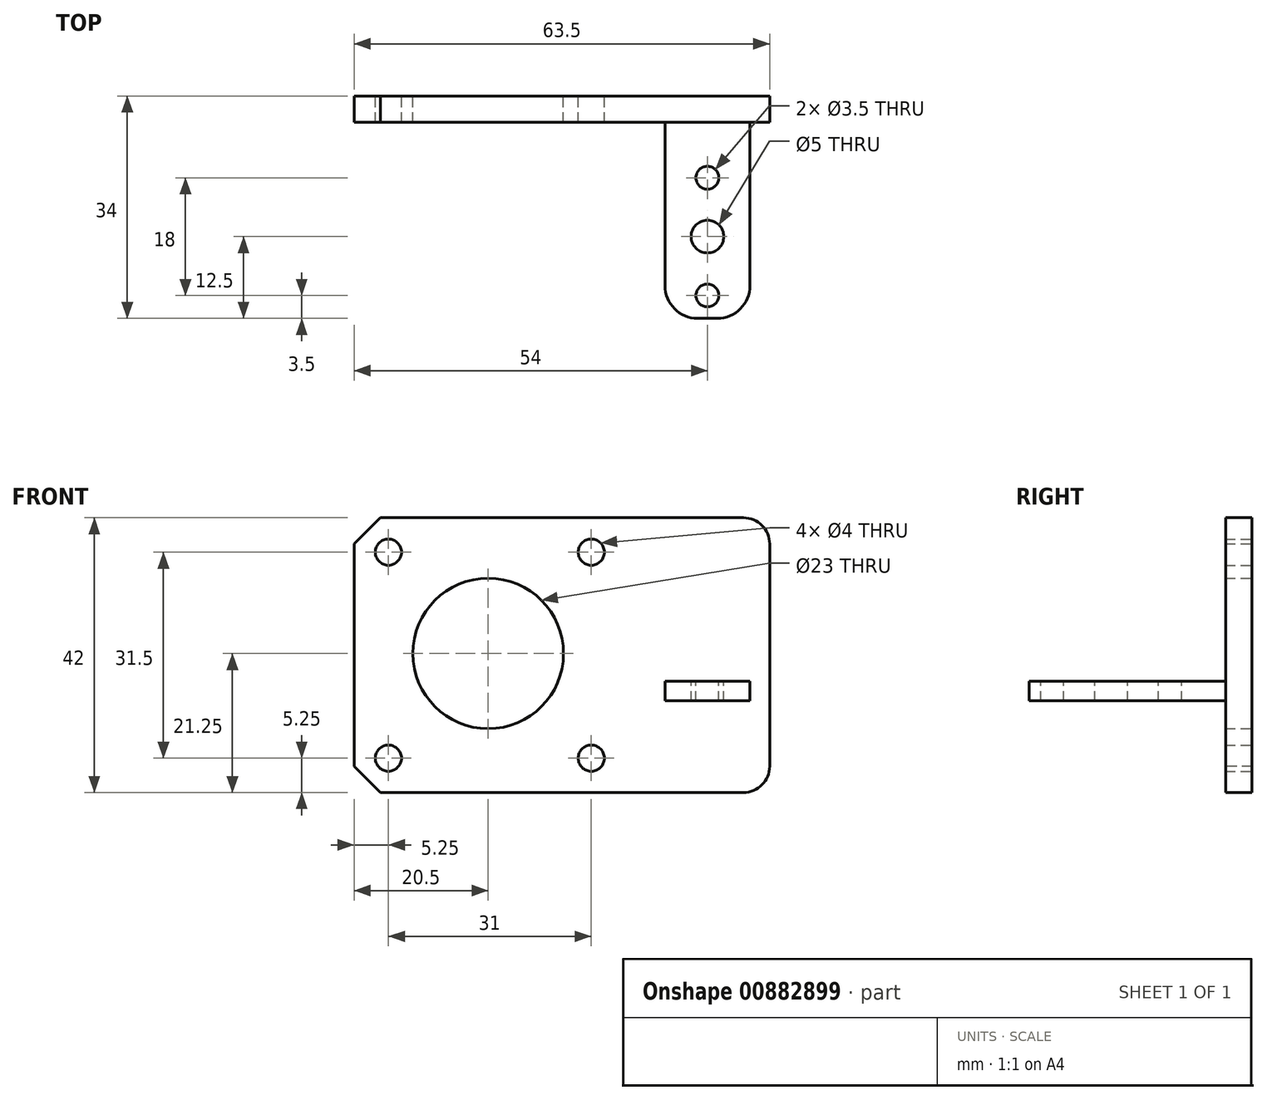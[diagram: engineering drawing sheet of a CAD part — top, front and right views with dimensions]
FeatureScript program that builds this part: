
annotation { "Feature Type Name" : "Feature", "Feature Type Description" : "" }
export const myFeature = defineFeature(function(context is Context, id is Id, definition is map)
    precondition{}
    {
        {
            var Q0;
            Q0=qCreatedBy(makeId("Front.planeOp"),FACE);
            var sketch = newSketch(context, id + "F0", { "sketchPlane" : qUnion([Q0])});
            skLineSegment(sketch, "E0.bottom", {"start": v(43, -21.25) * mm, "end": v(-20.5, -21.25) * mm});
            skLineSegment(sketch, "E0.top", {"start": v(43, 20.75) * mm, "end": v(-20.5, 20.75) * mm});
            skLineSegment(sketch, "E0.left", {"start": v(43, -21.25) * mm, "end": v(43, 20.75) * mm});
            skLineSegment(sketch, "E0.right", {"start": v(-20.5, -21.25) * mm, "end": v(-20.5, 20.75) * mm});
            skPoint(sketch, "E0.middle", {"position": v(0, 0) * mm});
            skCircle(sketch, "E1", {"center": v(0, 0) * mm, "radius": 11.5 * mm});
            skCircle(sketch, "E2", {"center": v(-15.25, 15.5) * mm, "radius": 2 * mm});
            skCircle(sketch, "E3", {"center": v(15.75, 15.5) * mm, "radius": 2 * mm});
            skCircle(sketch, "E4", {"center": v(-15.25, -16) * mm, "radius": 2 * mm});
            skCircle(sketch, "E5", {"center": v(15.75, -16) * mm, "radius": 2 * mm});
            skSolve(sketch);
        }
        {
            var Q0;
            Q0=makeQuery(id+"F0.imprint","IMPRINT",FACE,{"disambiguationData":[TD([[makeQuery(id+"F0.imprint","IMPRINT",EDGE,{"derivedFrom":sQuery(id+"F0.wireOp",EDGE,"E0.bottom")}),-1.0]])]});
            extrude(context, id + "F1", {"entities" : qUnion([Q0]), "depth" : 4 * mm, "offsetDistance" : 25 * mm});
        }
        {
            var Q0;
            Q0=makeQuery(id+"F1.opExtrude","SWEPT_EDGE",EDGE,{"disambiguationData":[OSD([sQuery(id+"F0.wireOp",EDGE,"E0.bottom"),sQuery(id+"F0.wireOp",EDGE,"E0.right")])]});
            var Q1;
            Q1=makeQuery(id+"F1.opExtrude","SWEPT_EDGE",EDGE,{"disambiguationData":[OSD([sQuery(id+"F0.wireOp",EDGE,"E0.top"),sQuery(id+"F0.wireOp",EDGE,"E0.right")])]});
            chamfer(context, id + "F2", {"entities" : qUnion([Q0, Q1]), "width" : 4 * mm, "tangentPropagation" : true});
        }
        {
            var Q0;
            Q0=makeQuery(id+"F1.opExtrude","CAP_FACE",FACE,{"disambiguationData":[OSD([sQuery(id+"F0.wireOp",EDGE,"E0.bottom"),sQuery(id+"F0.wireOp",EDGE,"E0.top"),sQuery(id+"F0.wireOp",EDGE,"E0.left"),sQuery(id+"F0.wireOp",EDGE,"E0.right"),sQuery(id+"F0.wireOp",EDGE,"E1"),sQuery(id+"F0.wireOp",EDGE,"E2"),sQuery(id+"F0.wireOp",EDGE,"E3"),sQuery(id+"F0.wireOp",EDGE,"E4"),sQuery(id+"F0.wireOp",EDGE,"E5")])],"isStart":false});
            var sketch = newSketch(context, id + "F3", { "sketchPlane" : qUnion([Q0])});
            skLineSegment(sketch, "E6.bottom", {"start": v(27, -4.25) * mm, "end": v(40, -4.25) * mm});
            skLineSegment(sketch, "E6.top", {"start": v(27, -7.25) * mm, "end": v(40, -7.25) * mm});
            skLineSegment(sketch, "E6.left", {"start": v(27, -4.25) * mm, "end": v(27, -7.25) * mm});
            skLineSegment(sketch, "E6.right", {"start": v(40, -4.25) * mm, "end": v(40, -7.25) * mm});
            skSolve(sketch);
        }
        {
            var Q0;
            Q0 = qSketchRegion(id + "F3", true);
            extrude(context, id + "F4", {"entities" : qUnion([Q0]), "operationType" : NewBodyOperationType.ADD, "depth" : 30 * mm, "offsetDistance" : 25 * mm});
        }
        {
            var Q0;
            Q0=makeQuery(id+"F4.opExtrude","CAP_EDGE",EDGE,{"disambiguationData":[OSD([sQuery(id+"F3.wireOp",EDGE,"E6.right")])],"isStart":false});
            var Q1;
            Q1=makeQuery(id+"F4.opExtrude","CAP_EDGE",EDGE,{"disambiguationData":[OSD([sQuery(id+"F3.wireOp",EDGE,"E6.left")])],"isStart":false});
            fillet(context, id + "F5", {"entities" : qUnion([Q0, Q1]), "radius" : 5 * mm, "tangentPropagation" : true, "allowEdgeOverflow" : false});
        }
        {
            var Q0;
            Q0=makeQuery(id+"F1.opExtrude","SWEPT_EDGE",EDGE,{"disambiguationData":[OSD([sQuery(id+"F0.wireOp",EDGE,"E0.top"),sQuery(id+"F0.wireOp",EDGE,"E0.left")])]});
            var Q1;
            Q1=makeQuery(id+"F1.opExtrude","SWEPT_EDGE",EDGE,{"disambiguationData":[OSD([sQuery(id+"F0.wireOp",EDGE,"E0.bottom"),sQuery(id+"F0.wireOp",EDGE,"E0.left")])]});
            fillet(context, id + "F6", {"entities" : qUnion([Q0, Q1]), "radius" : 4 * mm, "tangentPropagation" : true, "allowEdgeOverflow" : false});
        }
        {
            var Q0;
            Q0=makeQuery(id+"F4.opExtrude","SWEPT_FACE",FACE,{"disambiguationData":[OSD([sQuery(id+"F3.wireOp",EDGE,"E6.bottom")])]});
            var sketch = newSketch(context, id + "F7", { "sketchPlane" : qUnion([Q0])});
            skCircle(sketch, "E7", {"center": v(33.5, -21.5) * mm, "radius": 2.5 * mm});
            skCircle(sketch, "E8", {"center": v(33.5, -30.5) * mm, "radius": 1.75 * mm});
            skCircle(sketch, "E9", {"center": v(33.5, -12.5) * mm, "radius": 1.75 * mm});
            skLineSegment(sketch, "E10", {"start": v(33.5, -4) * mm, "end": v(33.5, -34) * mm, "construction": true});
            skSolve(sketch);
        }
        {
            var Q0;
            Q0 = qSketchRegion(id + "F7", true);
            extrude(context, id + "F8", {"entities" : qUnion([Q0]), "operationType" : NewBodyOperationType.REMOVE, "endBound" : BoundingType.UP_TO_NEXT, "oppositeDirection" : true, "depth" : 25 * mm, "offsetDistance" : 25 * mm});
        }
    });
